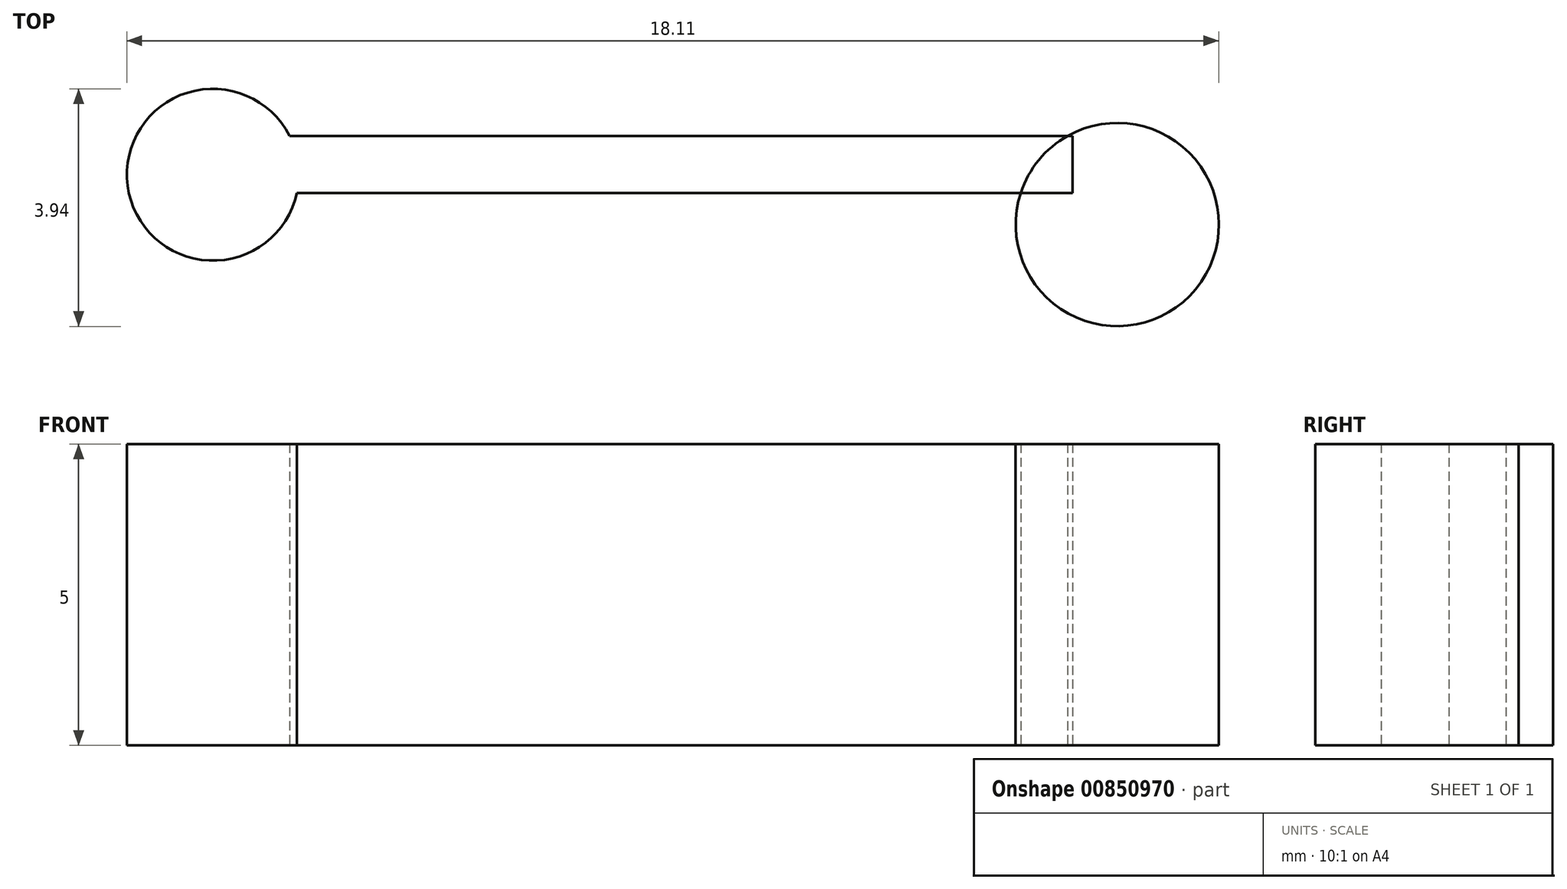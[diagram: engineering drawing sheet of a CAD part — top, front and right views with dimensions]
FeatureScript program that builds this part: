
annotation { "Feature Type Name" : "Feature", "Feature Type Description" : "" }
export const myFeature = defineFeature(function(context is Context, id is Id, definition is map)
    precondition{}
    {
        {
            var Q0;
            Q0=qCreatedBy(makeId("Top.planeOp"),FACE);
            var sketch = newSketch(context, id + "F0", { "sketchPlane" : qUnion([Q0])});
            skCircle(sketch, "E0", {"center": v(-9.75, 0.83) * mm, "radius": 1.43 * mm});
            skCircle(sketch, "E1", {"center": v(5.25, 0) * mm, "radius": 1.69 * mm});
            skLineSegment(sketch, "E2.bottom", {"start": v(-10.5, 1.47) * mm, "end": v(4.5, 1.47) * mm});
            skLineSegment(sketch, "E2.top", {"start": v(-10.5, 0.53) * mm, "end": v(4.5, 0.53) * mm});
            skLineSegment(sketch, "E2.left", {"start": v(-10.5, 1.47) * mm, "end": v(-10.5, 0.53) * mm});
            skLineSegment(sketch, "E2.right", {"start": v(4.5, 1.47) * mm, "end": v(4.5, 0.53) * mm});
            skSolve(sketch);
        }
        {
            var Q0;
            {var subQ5=sQuery(id+"F0.wireOp",EDGE,"E2.right");Q0=makeQuery(id+"F0.imprint","IMPRINT",FACE,{"disambiguationData":[TD([[makeQuery(id+"F0.imprint","IMPRINT",EDGE,{"derivedFrom":subQ5}),1.0]])]});}
            var Q1;
            {var subQ0=sQuery(id+"F0.wireOp",EDGE,"E2.bottom");var subQ1=sQuery(id+"F0.wireOp",EDGE,"E0");var subQ2=makeQuery(id+"F0.imprint","INTERSECT",VERTEX,{"derivedFrom":[subQ1,subQ0]});Q1=makeQuery(id+"F0.imprint","IMPRINT",FACE,{"disambiguationData":[TD([[makeQuery(id+"F0.imprint","IMPRINT",EDGE,{"disambiguationData":[TD([[subQ2,1.0]])],"derivedFrom":subQ1}),-1.0]])]});}
            var Q2;
            {var subQ5=sQuery(id+"F0.wireOp",EDGE,"E2.left");Q2=makeQuery(id+"F0.imprint","IMPRINT",FACE,{"disambiguationData":[TD([[makeQuery(id+"F0.imprint","IMPRINT",EDGE,{"derivedFrom":subQ5}),-1.0]])]});}
            var Q3;
            {var subQ5=sQuery(id+"F0.wireOp",EDGE,"E2.left");Q3=makeQuery(id+"F0.imprint","IMPRINT",FACE,{"disambiguationData":[TD([[makeQuery(id+"F0.imprint","IMPRINT",EDGE,{"derivedFrom":subQ5}),1.0]])]});}
            extrude(context, id + "F1", {"entities" : qUnion([Q0, Q1, Q2, Q3]), "depth" : 5 * mm, "offsetDistance" : 25 * mm});
        }
    });
